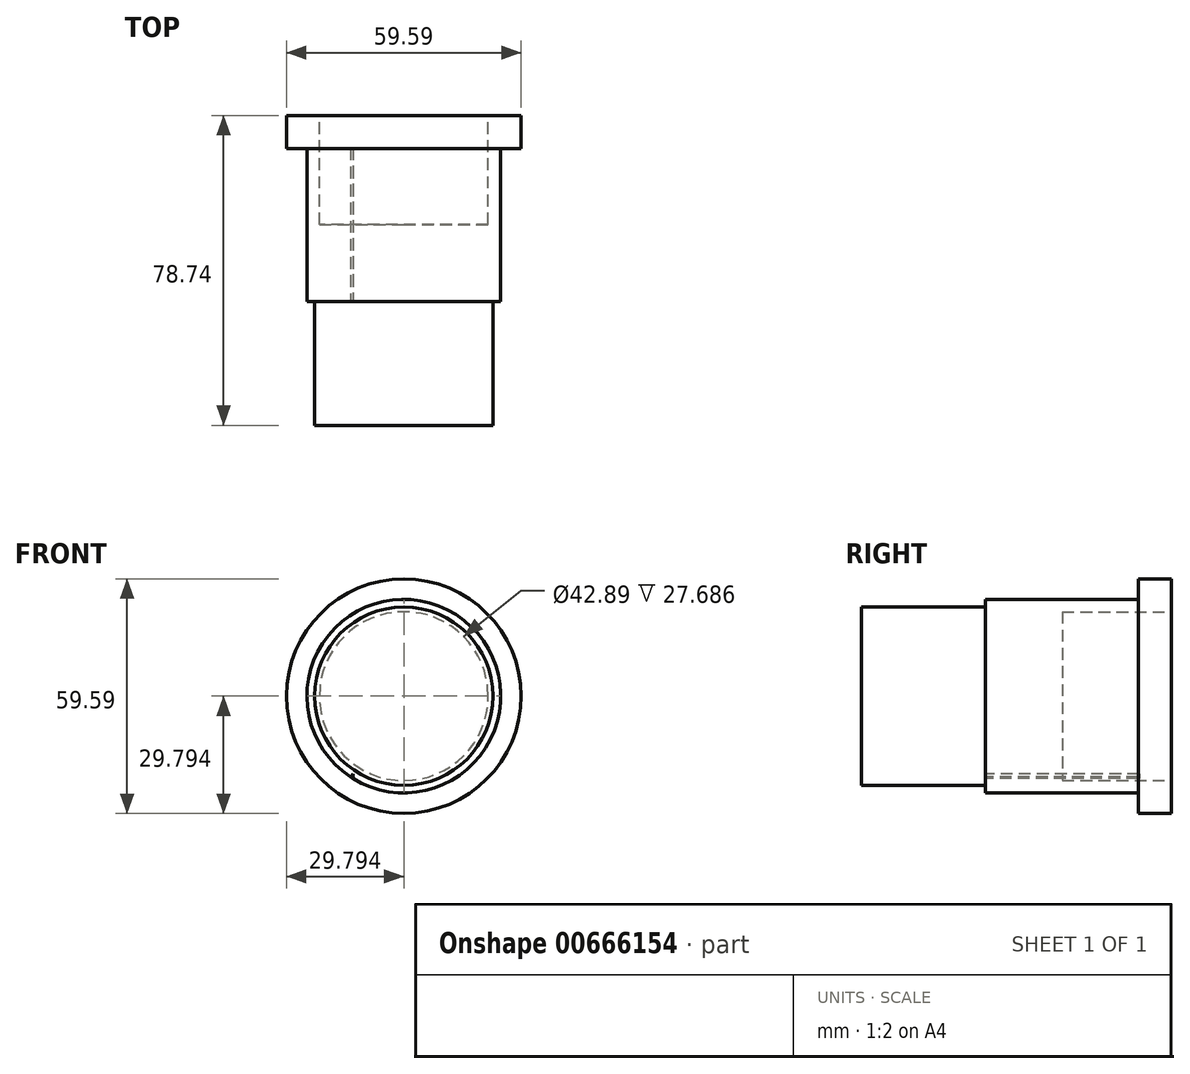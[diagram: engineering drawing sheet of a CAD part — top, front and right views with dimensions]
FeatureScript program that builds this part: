
annotation { "Feature Type Name" : "Feature", "Feature Type Description" : "" }
export const myFeature = defineFeature(function(context is Context, id is Id, definition is map)
    precondition{}
    {
        {
            var Q0;
            Q0=qCreatedBy(makeId("Front.planeOp"),FACE);
            var sketch = newSketch(context, id + "F0", { "sketchPlane" : qUnion([Q0])});
            skCircle(sketch, "E0", {"center": v(-5.35, 4) * mm, "radius": 29.8 * mm});
            skSolve(sketch);
        }
        {
            var Q0;
            Q0=makeQuery(id+"F0.imprint","IMPRINT",FACE,{"disambiguationData":[TD([[makeQuery(id+"F0.imprint","IMPRINT",EDGE,{"derivedFrom":sQuery(id+"F0.wireOp",EDGE,"E0")}),1.0]])]});
            extrude(context, id + "F1", {"entities" : qUnion([Q0]), "depth" : 8.38 * mm, "offsetDistance" : 25.4 * mm});
        }
        {
            var Q0;
            Q0=makeQuery(id+"F1.opExtrude","CAP_FACE",FACE,{"disambiguationData":[OSD([sQuery(id+"F0.wireOp",EDGE,"E0")])],"isStart":false});
            var sketch = newSketch(context, id + "F2", { "sketchPlane" : qUnion([Q0])});
            skCircle(sketch, "E1", {"center": v(-5.35, 4) * mm, "radius": 24.6 * mm});
            skSolve(sketch);
        }
        {
            var Q0;
            Q0=makeQuery(id+"F2.imprint","IMPRINT",FACE,{"disambiguationData":[TD([[makeQuery(id+"F2.imprint","IMPRINT",EDGE,{"derivedFrom":sQuery(id+"F2.wireOp",EDGE,"E1")}),1.0]])]});
            extrude(context, id + "F3", {"entities" : qUnion([Q0]), "operationType" : NewBodyOperationType.ADD, "depth" : 38.86 * mm, "offsetDistance" : 25.4 * mm});
        }
        {
            var Q0;
            Q0=makeQuery(id+"F3.opExtrude","CAP_FACE",FACE,{"disambiguationData":[OSD([sQuery(id+"F2.wireOp",EDGE,"E1")])],"isStart":false});
            var sketch = newSketch(context, id + "F4", { "sketchPlane" : qUnion([Q0])});
            skCircle(sketch, "E2", {"center": v(-5.35, 4) * mm, "radius": 22.66 * mm});
            skSolve(sketch);
        }
        {
            var Q0;
            Q0 = qSketchRegion(id + "F4", true);
            extrude(context, id + "F5", {"entities" : qUnion([Q0]), "operationType" : NewBodyOperationType.ADD, "depth" : 31.5 * mm, "offsetDistance" : 25.4 * mm});
        }
        {
            var Q0;
            Q0=makeQuery(id+"F3.opExtrude","CAP_FACE",FACE,{"disambiguationData":[OSD([sQuery(id+"F2.wireOp",EDGE,"E1")])],"isStart":false});
            var sketch = newSketch(context, id + "F6", { "sketchPlane" : qUnion([Q0])});
            skLineSegment(sketch, "E3", {"start": v(-18.27, -15.79) * mm, "end": v(-18.27, -17.35) * mm});
            skLineSegment(sketch, "E4", {"start": v(-18.27, -17.35) * mm, "end": v(-19.16, -16.77) * mm});
            skLineSegment(sketch, "E5", {"start": v(-19.16, -16.77) * mm, "end": v(-18.27, -15.79) * mm});
            skLineSegment(sketch, "E6.1.0", {"start": v(-15.02, -17.57) * mm, "end": v(-14.78, -19.11) * mm});
            skLineSegment(sketch, "E6.1.1", {"start": v(-14.78, -19.11) * mm, "end": v(-15.74, -18.67) * mm});
            skLineSegment(sketch, "E6.1.2", {"start": v(-15.74, -18.67) * mm, "end": v(-15.02, -17.57) * mm});
            skLineSegment(sketch, "E6.2.0", {"start": v(-11.53, -18.82) * mm, "end": v(-11.04, -20.3) * mm});
            skLineSegment(sketch, "E6.2.1", {"start": v(-11.04, -20.3) * mm, "end": v(-12.07, -20.02) * mm});
            skLineSegment(sketch, "E6.2.2", {"start": v(-12.07, -20.02) * mm, "end": v(-11.53, -18.82) * mm});
            skLineSegment(sketch, "E6.3.0", {"start": v(-7.88, -19.5) * mm, "end": v(-7.17, -20.9) * mm});
            skLineSegment(sketch, "E6.3.1", {"start": v(-7.17, -20.9) * mm, "end": v(-8.23, -20.78) * mm});
            skLineSegment(sketch, "E6.3.2", {"start": v(-8.23, -20.78) * mm, "end": v(-7.88, -19.5) * mm});
            skLineSegment(sketch, "E6.4.0", {"start": v(-4.18, -19.61) * mm, "end": v(-3.26, -20.88) * mm});
            skLineSegment(sketch, "E6.4.1", {"start": v(-3.26, -20.88) * mm, "end": v(-4.32, -20.92) * mm});
            skLineSegment(sketch, "E6.4.2", {"start": v(-4.32, -20.92) * mm, "end": v(-4.18, -19.61) * mm});
            skLineSegment(sketch, "E6.5.0", {"start": v(-0.5, -19.14) * mm, "end": v(0.6, -20.24) * mm});
            skLineSegment(sketch, "E6.5.1", {"start": v(0.6, -20.24) * mm, "end": v(-0.44, -20.45) * mm});
            skLineSegment(sketch, "E6.5.2", {"start": v(-0.44, -20.45) * mm, "end": v(-0.5, -19.14) * mm});
            skLineSegment(sketch, "E6.6.0", {"start": v(3.06, -18.1) * mm, "end": v(4.33, -19.01) * mm});
            skLineSegment(sketch, "E6.6.1", {"start": v(4.33, -19.01) * mm, "end": v(3.33, -19.39) * mm});
            skLineSegment(sketch, "E6.6.2", {"start": v(3.33, -19.39) * mm, "end": v(3.06, -18.1) * mm});
            skLineSegment(sketch, "E6.7.0", {"start": v(6.41, -16.5) * mm, "end": v(7.8, -17.22) * mm});
            skLineSegment(sketch, "E6.7.1", {"start": v(7.8, -17.22) * mm, "end": v(6.88, -17.74) * mm});
            skLineSegment(sketch, "E6.7.2", {"start": v(6.88, -17.74) * mm, "end": v(6.41, -16.5) * mm});
            skLineSegment(sketch, "E6.8.0", {"start": v(9.47, -14.42) * mm, "end": v(10.96, -14.9) * mm});
            skLineSegment(sketch, "E6.8.1", {"start": v(10.96, -14.9) * mm, "end": v(10.13, -15.56) * mm});
            skLineSegment(sketch, "E6.8.2", {"start": v(10.13, -15.56) * mm, "end": v(9.47, -14.42) * mm});
            skLineSegment(sketch, "E6.9.0", {"start": v(12.17, -11.87) * mm, "end": v(13.72, -12.11) * mm});
            skLineSegment(sketch, "E6.9.1", {"start": v(13.72, -12.11) * mm, "end": v(13, -12.9) * mm});
            skLineSegment(sketch, "E6.9.2", {"start": v(13, -12.9) * mm, "end": v(12.17, -11.87) * mm});
            skLineSegment(sketch, "E6.10.0", {"start": v(14.44, -8.93) * mm, "end": v(16, -8.93) * mm});
            skLineSegment(sketch, "E6.10.1", {"start": v(16, -8.93) * mm, "end": v(15.41, -9.82) * mm});
            skLineSegment(sketch, "E6.10.2", {"start": v(15.41, -9.82) * mm, "end": v(14.44, -8.93) * mm});
            skLineSegment(sketch, "E6.11.0", {"start": v(16.22, -5.68) * mm, "end": v(17.76, -5.44) * mm});
            skLineSegment(sketch, "E6.11.1", {"start": v(17.76, -5.44) * mm, "end": v(17.32, -6.4) * mm});
            skLineSegment(sketch, "E6.11.2", {"start": v(17.32, -6.4) * mm, "end": v(16.22, -5.68) * mm});
            skLineSegment(sketch, "E6.12.0", {"start": v(17.46, -2.19) * mm, "end": v(18.95, -1.7) * mm});
            skLineSegment(sketch, "E6.12.1", {"start": v(18.95, -1.7) * mm, "end": v(18.67, -2.73) * mm});
            skLineSegment(sketch, "E6.12.2", {"start": v(18.67, -2.73) * mm, "end": v(17.46, -2.19) * mm});
            skLineSegment(sketch, "E6.13.0", {"start": v(18.15, 1.46) * mm, "end": v(19.55, 2.17) * mm});
            skLineSegment(sketch, "E6.13.1", {"start": v(19.55, 2.17) * mm, "end": v(19.42, 1.1) * mm});
            skLineSegment(sketch, "E6.13.2", {"start": v(19.42, 1.1) * mm, "end": v(18.15, 1.46) * mm});
            skLineSegment(sketch, "E6.14.0", {"start": v(18.26, 5.16) * mm, "end": v(19.53, 6.08) * mm});
            skLineSegment(sketch, "E6.14.1", {"start": v(19.53, 6.08) * mm, "end": v(19.57, 5.02) * mm});
            skLineSegment(sketch, "E6.14.2", {"start": v(19.57, 5.02) * mm, "end": v(18.26, 5.16) * mm});
            skLineSegment(sketch, "E6.15.0", {"start": v(17.79, 8.84) * mm, "end": v(18.9, 9.95) * mm});
            skLineSegment(sketch, "E6.15.1", {"start": v(18.9, 9.95) * mm, "end": v(19.1, 8.9) * mm});
            skLineSegment(sketch, "E6.15.2", {"start": v(19.1, 8.9) * mm, "end": v(17.79, 8.84) * mm});
            skLineSegment(sketch, "E6.16.0", {"start": v(16.74, 12.4) * mm, "end": v(17.66, 13.67) * mm});
            skLineSegment(sketch, "E6.16.1", {"start": v(17.66, 13.67) * mm, "end": v(18.03, 12.67) * mm});
            skLineSegment(sketch, "E6.16.2", {"start": v(18.03, 12.67) * mm, "end": v(16.74, 12.4) * mm});
            skLineSegment(sketch, "E6.17.0", {"start": v(15.16, 15.75) * mm, "end": v(15.87, 17.15) * mm});
            skLineSegment(sketch, "E6.17.1", {"start": v(15.87, 17.15) * mm, "end": v(16.39, 16.22) * mm});
            skLineSegment(sketch, "E6.17.2", {"start": v(16.39, 16.22) * mm, "end": v(15.16, 15.75) * mm});
            skLineSegment(sketch, "E6.18.0", {"start": v(13.06, 18.81) * mm, "end": v(13.55, 20.3) * mm});
            skLineSegment(sketch, "E6.18.1", {"start": v(13.55, 20.3) * mm, "end": v(14.2, 19.47) * mm});
            skLineSegment(sketch, "E6.18.2", {"start": v(14.2, 19.47) * mm, "end": v(13.06, 18.81) * mm});
            skLineSegment(sketch, "E6.19.0", {"start": v(10.52, 21.51) * mm, "end": v(10.76, 23.06) * mm});
            skLineSegment(sketch, "E6.19.1", {"start": v(10.76, 23.06) * mm, "end": v(11.55, 22.34) * mm});
            skLineSegment(sketch, "E6.19.2", {"start": v(11.55, 22.34) * mm, "end": v(10.52, 21.51) * mm});
            skLineSegment(sketch, "E6.20.0", {"start": v(7.58, 23.78) * mm, "end": v(7.58, 25.34) * mm});
            skLineSegment(sketch, "E6.20.1", {"start": v(7.58, 25.34) * mm, "end": v(8.47, 24.75) * mm});
            skLineSegment(sketch, "E6.20.2", {"start": v(8.47, 24.75) * mm, "end": v(7.58, 23.78) * mm});
            skLineSegment(sketch, "E6.21.0", {"start": v(4.33, 25.56) * mm, "end": v(4.08, 27.1) * mm});
            skLineSegment(sketch, "E6.21.1", {"start": v(4.08, 27.1) * mm, "end": v(5.05, 26.66) * mm});
            skLineSegment(sketch, "E6.21.2", {"start": v(5.05, 26.66) * mm, "end": v(4.33, 25.56) * mm});
            skLineSegment(sketch, "E6.22.0", {"start": v(0.84, 26.8) * mm, "end": v(0.35, 28.3) * mm});
            skLineSegment(sketch, "E6.22.1", {"start": v(0.35, 28.3) * mm, "end": v(1.38, 28) * mm});
            skLineSegment(sketch, "E6.22.2", {"start": v(1.38, 28) * mm, "end": v(0.84, 26.8) * mm});
            skLineSegment(sketch, "E6.23.0", {"start": v(-2.8, 27.5) * mm, "end": v(-3.52, 28.89) * mm});
            skLineSegment(sketch, "E6.23.1", {"start": v(-3.52, 28.89) * mm, "end": v(-2.46, 28.76) * mm});
            skLineSegment(sketch, "E6.23.2", {"start": v(-2.46, 28.76) * mm, "end": v(-2.8, 27.5) * mm});
            skLineSegment(sketch, "E6.24.0", {"start": v(-6.52, 27.6) * mm, "end": v(-7.44, 28.87) * mm});
            skLineSegment(sketch, "E6.24.1", {"start": v(-7.44, 28.87) * mm, "end": v(-6.37, 28.91) * mm});
            skLineSegment(sketch, "E6.24.2", {"start": v(-6.37, 28.91) * mm, "end": v(-6.52, 27.6) * mm});
            skLineSegment(sketch, "E6.25.0", {"start": v(-10.2, 27.13) * mm, "end": v(-11.3, 28.23) * mm});
            skLineSegment(sketch, "E6.25.1", {"start": v(-11.3, 28.23) * mm, "end": v(-10.26, 28.44) * mm});
            skLineSegment(sketch, "E6.25.2", {"start": v(-10.26, 28.44) * mm, "end": v(-10.2, 27.13) * mm});
            skLineSegment(sketch, "E6.26.0", {"start": v(-13.75, 26.08) * mm, "end": v(-15.02, 27) * mm});
            skLineSegment(sketch, "E6.26.1", {"start": v(-15.02, 27) * mm, "end": v(-14.02, 27.37) * mm});
            skLineSegment(sketch, "E6.26.2", {"start": v(-14.02, 27.37) * mm, "end": v(-13.75, 26.08) * mm});
            skLineSegment(sketch, "E6.27.0", {"start": v(-17.1, 24.5) * mm, "end": v(-18.5, 25.2) * mm});
            skLineSegment(sketch, "E6.27.1", {"start": v(-18.5, 25.2) * mm, "end": v(-17.57, 25.73) * mm});
            skLineSegment(sketch, "E6.27.2", {"start": v(-17.57, 25.73) * mm, "end": v(-17.1, 24.5) * mm});
            skLineSegment(sketch, "E6.28.0", {"start": v(-20.17, 22.4) * mm, "end": v(-21.66, 22.89) * mm});
            skLineSegment(sketch, "E6.28.1", {"start": v(-21.66, 22.89) * mm, "end": v(-20.82, 23.55) * mm});
            skLineSegment(sketch, "E6.28.2", {"start": v(-20.82, 23.55) * mm, "end": v(-20.17, 22.4) * mm});
            skLineSegment(sketch, "E6.29.0", {"start": v(-22.86, 19.86) * mm, "end": v(-24.4, 20.1) * mm});
            skLineSegment(sketch, "E6.29.1", {"start": v(-24.4, 20.1) * mm, "end": v(-23.69, 20.89) * mm});
            skLineSegment(sketch, "E6.29.2", {"start": v(-23.69, 20.89) * mm, "end": v(-22.86, 19.86) * mm});
            skLineSegment(sketch, "E6.30.0", {"start": v(-25.13, 16.92) * mm, "end": v(-26.7, 16.92) * mm});
            skLineSegment(sketch, "E6.30.1", {"start": v(-26.7, 16.92) * mm, "end": v(-26.1, 17.81) * mm});
            skLineSegment(sketch, "E6.30.2", {"start": v(-26.1, 17.81) * mm, "end": v(-25.13, 16.92) * mm});
            skLineSegment(sketch, "E6.31.0", {"start": v(-26.9, 13.67) * mm, "end": v(-28.45, 13.42) * mm});
            skLineSegment(sketch, "E6.31.1", {"start": v(-28.45, 13.42) * mm, "end": v(-28.01, 14.4) * mm});
            skLineSegment(sketch, "E6.31.2", {"start": v(-28.01, 14.4) * mm, "end": v(-26.9, 13.67) * mm});
            skLineSegment(sketch, "E6.32.0", {"start": v(-28.16, 10.18) * mm, "end": v(-29.65, 9.7) * mm});
            skLineSegment(sketch, "E6.32.1", {"start": v(-29.65, 9.7) * mm, "end": v(-29.36, 10.72) * mm});
            skLineSegment(sketch, "E6.32.2", {"start": v(-29.36, 10.72) * mm, "end": v(-28.16, 10.18) * mm});
            skLineSegment(sketch, "E6.33.0", {"start": v(-28.84, 6.53) * mm, "end": v(-30.24, 5.82) * mm});
            skLineSegment(sketch, "E6.33.1", {"start": v(-30.24, 5.82) * mm, "end": v(-30.12, 6.88) * mm});
            skLineSegment(sketch, "E6.33.2", {"start": v(-30.12, 6.88) * mm, "end": v(-28.84, 6.53) * mm});
            skLineSegment(sketch, "E6.34.0", {"start": v(-28.95, 2.83) * mm, "end": v(-30.22, 1.9) * mm});
            skLineSegment(sketch, "E6.34.1", {"start": v(-30.22, 1.9) * mm, "end": v(-30.26, 2.97) * mm});
            skLineSegment(sketch, "E6.34.2", {"start": v(-30.26, 2.97) * mm, "end": v(-28.95, 2.83) * mm});
            skLineSegment(sketch, "E6.35.0", {"start": v(-28.48, -0.85) * mm, "end": v(-29.58, -1.96) * mm});
            skLineSegment(sketch, "E6.35.1", {"start": v(-29.58, -1.96) * mm, "end": v(-29.8, -0.92) * mm});
            skLineSegment(sketch, "E6.35.2", {"start": v(-29.8, -0.92) * mm, "end": v(-28.48, -0.85) * mm});
            skLineSegment(sketch, "E6.36.0", {"start": v(-27.43, -4.41) * mm, "end": v(-28.35, -5.68) * mm});
            skLineSegment(sketch, "E6.36.1", {"start": v(-28.35, -5.68) * mm, "end": v(-28.73, -4.68) * mm});
            skLineSegment(sketch, "E6.36.2", {"start": v(-28.73, -4.68) * mm, "end": v(-27.43, -4.41) * mm});
            skLineSegment(sketch, "E6.37.0", {"start": v(-25.85, -7.76) * mm, "end": v(-26.56, -9.16) * mm});
            skLineSegment(sketch, "E6.37.1", {"start": v(-26.56, -9.16) * mm, "end": v(-27.08, -8.23) * mm});
            skLineSegment(sketch, "E6.37.2", {"start": v(-27.08, -8.23) * mm, "end": v(-25.85, -7.76) * mm});
            skLineSegment(sketch, "E6.38.0", {"start": v(-23.76, -10.83) * mm, "end": v(-24.24, -12.31) * mm});
            skLineSegment(sketch, "E6.38.1", {"start": v(-24.24, -12.31) * mm, "end": v(-24.9, -11.48) * mm});
            skLineSegment(sketch, "E6.38.2", {"start": v(-24.9, -11.48) * mm, "end": v(-23.76, -10.83) * mm});
            skLineSegment(sketch, "E6.39.0", {"start": v(-21.21, -13.52) * mm, "end": v(-21.46, -15.07) * mm});
            skLineSegment(sketch, "E6.39.1", {"start": v(-21.46, -15.07) * mm, "end": v(-22.24, -14.35) * mm});
            skLineSegment(sketch, "E6.39.2", {"start": v(-22.24, -14.35) * mm, "end": v(-21.21, -13.52) * mm});
            skPoint(sketch, "E6.center", {"position": v(-5.35, 4) * mm});
            skSolve(sketch);
        }
        {
            var Q0;
            {var subQ0=sQuery(id+"F6.wireOp",EDGE,"E5");var subQ1=sQuery(id+"F6.wireOp",EDGE,"E3");var subQ2=makeQuery(id+"F6.imprint","INTERSECT",VERTEX,{"derivedFrom":[subQ1,subQ0]});Q0=makeQuery(id+"F6.imprint","IMPRINT",FACE,{"disambiguationData":[TD([[makeQuery(id+"F6.imprint","IMPRINT",EDGE,{"disambiguationData":[TD([[subQ2,-1.0]])],"derivedFrom":subQ1}),-1.0]])]});}
            extrude(context, id + "F7", {"entities" : qUnion([Q0]), "operationType" : NewBodyOperationType.REMOVE, "oppositeDirection" : true, "depth" : 39.12 * mm, "offsetDistance" : 25.4 * mm});
        }
        {
            var Q0;
            Q0=makeQuery(id+"F1.opExtrude","CAP_FACE",FACE,{"disambiguationData":[OSD([sQuery(id+"F0.wireOp",EDGE,"E0")])],"isStart":true});
            var sketch = newSketch(context, id + "F8", { "sketchPlane" : qUnion([Q0])});
            skCircle(sketch, "E7", {"center": v(5.35, 4) * mm, "radius": 21.44 * mm});
            skSolve(sketch);
        }
        {
            var Q0;
            Q0=makeQuery(id+"F8.imprint","IMPRINT",FACE,{"disambiguationData":[TD([[makeQuery(id+"F8.imprint","IMPRINT",EDGE,{"derivedFrom":sQuery(id+"F8.wireOp",EDGE,"E7")}),1.0]])]});
            extrude(context, id + "F9", {"entities" : qUnion([Q0]), "operationType" : NewBodyOperationType.REMOVE, "oppositeDirection" : true, "depth" : 2.3 * mm, "offsetDistance" : 25.4 * mm});
        }
        {
            var Q0;
            Q0=makeQuery(id+"F9.boolean.opBoolean","COPY",FACE,{"derivedFrom":makeQuery(id+"F9.opExtrude","CAP_FACE",FACE,{"disambiguationData":[OSD([sQuery(id+"F8.wireOp",EDGE,"E7")])],"isStart":false})});
            extrude(context, id + "F10", {"entities" : qUnion([Q0]), "operationType" : NewBodyOperationType.REMOVE, "oppositeDirection" : true, "depth" : 25.4 * mm, "offsetDistance" : 25.4 * mm});
        }
    });
